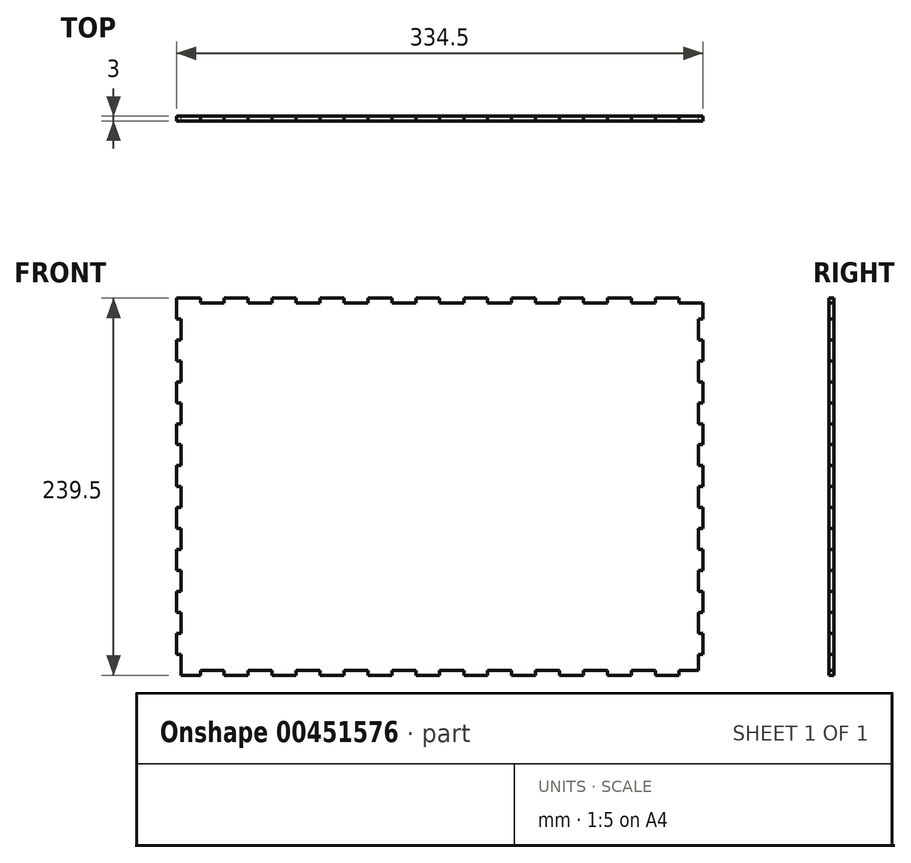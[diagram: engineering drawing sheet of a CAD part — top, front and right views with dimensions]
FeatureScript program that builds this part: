
annotation { "Feature Type Name" : "Feature", "Feature Type Description" : "" }
export const myFeature = defineFeature(function(context is Context, id is Id, definition is map)
    precondition{}
    {
        {
            var Q0;
            Q0=qCreatedBy(makeId("Front.planeOp"),FACE);
            var sketch = newSketch(context, id + "F0", { "sketchPlane" : qUnion([Q0])});
            skLineSegment(sketch, "E0.top", {"start": v(152.05, 119.75) * mm, "end": v(136.85, 119.75) * mm});
            skLineSegment(sketch, "E0.left", {"start": v(167.25, -117) * mm, "end": v(167.25, -116.75) * mm});
            skLineSegment(sketch, "E0.right", {"start": v(-167.25, -106.45) * mm, "end": v(-167.25, -93.15) * mm});
            skPoint(sketch, "E0.middle", {"position": v(0, 0) * mm});
            skLineSegment(sketch, "E1", {"start": v(-152.05, 116.75) * mm, "end": v(-136.85, 116.75) * mm});
            skLineSegment(sketch, "E2", {"start": v(-152.05, 119.75) * mm, "end": v(-152.05, 116.75) * mm});
            skLineSegment(sketch, "E3", {"start": v(-136.85, 119.75) * mm, "end": v(-136.85, 116.75) * mm});
            skLineSegment(sketch, "E4", {"start": v(-106.45, 119.75) * mm, "end": v(-106.45, 116.75) * mm});
            skLineSegment(sketch, "E5", {"start": v(-91.25, 119.75) * mm, "end": v(-91.25, 116.75) * mm});
            skLineSegment(sketch, "E6", {"start": v(-76.05, 119.75) * mm, "end": v(-76.05, 116.75) * mm});
            skLineSegment(sketch, "E7", {"start": v(-60.85, 119.75) * mm, "end": v(-60.85, 116.75) * mm});
            skLineSegment(sketch, "E8", {"start": v(-30.45, 119.75) * mm, "end": v(-30.45, 116.75) * mm});
            skLineSegment(sketch, "E9", {"start": v(-15.25, 119.75) * mm, "end": v(-15.25, 116.75) * mm});
            skLineSegment(sketch, "E10", {"start": v(-121.65, 119.75) * mm, "end": v(-121.65, 116.75) * mm});
            skLineSegment(sketch, "E11", {"start": v(-45.65, 119.75) * mm, "end": v(-45.65, 116.75) * mm});
            skLineSegment(sketch, "E12", {"start": v(-0.05, 119.75) * mm, "end": v(-0.05, 116.75) * mm});
            skLineSegment(sketch, "E13.MirrorCS", {"start": v(76.05, 119.75) * mm, "end": v(76.05, 116.75) * mm});
            skLineSegment(sketch, "E14.MirrorCS", {"start": v(60.85, 119.75) * mm, "end": v(60.85, 116.75) * mm});
            skLineSegment(sketch, "E15.MirrorCS", {"start": v(30.45, 119.75) * mm, "end": v(30.45, 116.75) * mm});
            skLineSegment(sketch, "E16.MirrorCS", {"start": v(121.65, 119.75) * mm, "end": v(121.65, 116.75) * mm});
            skLineSegment(sketch, "E17.MirrorCS", {"start": v(45.65, 119.75) * mm, "end": v(45.65, 116.75) * mm});
            skLineSegment(sketch, "E18.MirrorCS", {"start": v(0.05, 119.75) * mm, "end": v(0.05, 116.75) * mm});
            skLineSegment(sketch, "E19.MirrorCS", {"start": v(152.05, 119.75) * mm, "end": v(152.05, 116.75) * mm});
            skLineSegment(sketch, "E20.MirrorCS", {"start": v(15.25, 119.75) * mm, "end": v(15.25, 116.75) * mm});
            skLineSegment(sketch, "E21.MirrorCS", {"start": v(136.85, 119.75) * mm, "end": v(136.85, 116.75) * mm});
            skLineSegment(sketch, "E22.MirrorCS", {"start": v(106.45, 119.75) * mm, "end": v(106.45, 116.75) * mm});
            skLineSegment(sketch, "E23.MirrorCS", {"start": v(91.25, 119.75) * mm, "end": v(91.25, 116.75) * mm});
            skLineSegment(sketch, "E24.MirrorCS", {"start": v(-167.25, 119.75) * mm, "end": v(-152.05, 119.75) * mm});
            skLineSegment(sketch, "E25.trimOffspring", {"start": v(-0.05, 119.75) * mm, "end": v(0.05, 119.75) * mm});
            skLineSegment(sketch, "E26.trimOffspring", {"start": v(-121.65, 119.75) * mm, "end": v(-136.85, 119.75) * mm});
            skLineSegment(sketch, "E27.trimOffspring", {"start": v(-0.05, 116.75) * mm, "end": v(0.05, 116.75) * mm});
            skLineSegment(sketch, "E28.trimOffspring", {"start": v(-106.45, 116.75) * mm, "end": v(-121.65, 116.75) * mm});
            skLineSegment(sketch, "E29.trimOffspring", {"start": v(-91.25, 119.75) * mm, "end": v(-106.45, 119.75) * mm});
            skLineSegment(sketch, "E30.trimOffspring", {"start": v(-76.05, 116.75) * mm, "end": v(-91.25, 116.75) * mm});
            skLineSegment(sketch, "E31.trimOffspring", {"start": v(-60.85, 119.75) * mm, "end": v(-76.05, 119.75) * mm});
            skLineSegment(sketch, "E32.trimOffspring", {"start": v(-30.45, 119.75) * mm, "end": v(-45.65, 119.75) * mm});
            skLineSegment(sketch, "E33.trimOffspring", {"start": v(-15.25, 116.75) * mm, "end": v(-30.45, 116.75) * mm});
            skLineSegment(sketch, "E34.trimOffspring", {"start": v(30.45, 116.75) * mm, "end": v(45.65, 116.75) * mm});
            skLineSegment(sketch, "E35.trimOffspring", {"start": v(0.05, 119.75) * mm, "end": v(-15.25, 119.75) * mm});
            skLineSegment(sketch, "E36.trimOffspring", {"start": v(15.25, 116.75) * mm, "end": v(-0.05, 116.75) * mm});
            skLineSegment(sketch, "E37.trimOffspring", {"start": v(30.45, 119.75) * mm, "end": v(15.25, 119.75) * mm});
            skLineSegment(sketch, "E38.trimOffspring", {"start": v(152.05, 116.75) * mm, "end": v(167.25, 116.75) * mm});
            skLineSegment(sketch, "E39.trimOffspring", {"start": v(60.85, 119.75) * mm, "end": v(45.65, 119.75) * mm});
            skLineSegment(sketch, "E40.trimOffspring", {"start": v(76.05, 116.75) * mm, "end": v(60.85, 116.75) * mm});
            skLineSegment(sketch, "E41.trimOffspring", {"start": v(91.25, 119.75) * mm, "end": v(76.05, 119.75) * mm});
            skLineSegment(sketch, "E42.trimOffspring", {"start": v(106.45, 116.75) * mm, "end": v(91.25, 116.75) * mm});
            skLineSegment(sketch, "E43.trimOffspring", {"start": v(121.65, 119.75) * mm, "end": v(106.45, 119.75) * mm});
            skLineSegment(sketch, "E44.trimOffspring", {"start": v(136.85, 116.75) * mm, "end": v(121.65, 116.75) * mm});
            skPoint(sketch, "E45.MirrorCS.start.orphan", {"position": v(167.25, 117) * mm});
            skPoint(sketch, "E46.orphan", {"position": v(167.25, 120) * mm});
            skPoint(sketch, "E47.orphan", {"position": v(167.25, 119.75) * mm});
            skLineSegment(sketch, "E48.MirrorCS", {"start": v(-0.05, -119.75) * mm, "end": v(-0.05, -116.75) * mm});
            skLineSegment(sketch, "E49.MirrorCS", {"start": v(0.05, -119.75) * mm, "end": v(0.05, -116.75) * mm});
            skLineSegment(sketch, "E50.MirrorCS", {"start": v(-0.05, -119.75) * mm, "end": v(0.05, -119.75) * mm});
            skLineSegment(sketch, "E51.MirrorCS", {"start": v(-0.05, -116.75) * mm, "end": v(0.05, -116.75) * mm});
            skLineSegment(sketch, "E52.MirrorCS", {"start": v(-164.25, -119.75) * mm, "end": v(-152.05, -119.75) * mm});
            skLineSegment(sketch, "E53.MirrorCS", {"start": v(121.65, -119.75) * mm, "end": v(121.65, -116.75) * mm});
            skLineSegment(sketch, "E54.MirrorCS", {"start": v(15.25, -119.75) * mm, "end": v(15.25, -116.75) * mm});
            skLineSegment(sketch, "E55.MirrorCS", {"start": v(-45.65, -119.75) * mm, "end": v(-45.65, -116.75) * mm});
            skLineSegment(sketch, "E56.MirrorCS", {"start": v(30.45, -119.75) * mm, "end": v(30.45, -116.75) * mm});
            skLineSegment(sketch, "E57.MirrorCS", {"start": v(-152.05, -119.75) * mm, "end": v(-152.05, -116.75) * mm});
            skLineSegment(sketch, "E58.MirrorCS", {"start": v(-136.85, -119.75) * mm, "end": v(-136.85, -116.75) * mm});
            skLineSegment(sketch, "E59.MirrorCS", {"start": v(-106.45, -119.75) * mm, "end": v(-106.45, -116.75) * mm});
            skLineSegment(sketch, "E60.MirrorCS", {"start": v(-91.25, -119.75) * mm, "end": v(-91.25, -116.75) * mm});
            skLineSegment(sketch, "E61.MirrorCS", {"start": v(-76.05, -119.75) * mm, "end": v(-76.05, -116.75) * mm});
            skLineSegment(sketch, "E62.MirrorCS", {"start": v(-60.85, -119.75) * mm, "end": v(-60.85, -116.75) * mm});
            skLineSegment(sketch, "E63.MirrorCS", {"start": v(-30.45, -119.75) * mm, "end": v(-30.45, -116.75) * mm});
            skLineSegment(sketch, "E64.MirrorCS", {"start": v(-15.25, -119.75) * mm, "end": v(-15.25, -116.75) * mm});
            skLineSegment(sketch, "E65.MirrorCS", {"start": v(-121.65, -119.75) * mm, "end": v(-121.65, -116.75) * mm});
            skLineSegment(sketch, "E66.MirrorCS", {"start": v(136.85, -119.75) * mm, "end": v(136.85, -116.75) * mm});
            skLineSegment(sketch, "E67.MirrorCS", {"start": v(106.45, -119.75) * mm, "end": v(106.45, -116.75) * mm});
            skLineSegment(sketch, "E68.MirrorCS", {"start": v(152.05, -119.75) * mm, "end": v(152.05, -116.75) * mm});
            skLineSegment(sketch, "E69.MirrorCS", {"start": v(76.05, -119.75) * mm, "end": v(76.05, -116.75) * mm});
            skLineSegment(sketch, "E70.MirrorCS", {"start": v(152.05, -116.75) * mm, "end": v(164.25, -116.75) * mm});
            skLineSegment(sketch, "E71.MirrorCS", {"start": v(91.25, -119.75) * mm, "end": v(91.25, -116.75) * mm});
            skLineSegment(sketch, "E72.MirrorCS", {"start": v(60.85, -119.75) * mm, "end": v(60.85, -116.75) * mm});
            skLineSegment(sketch, "E73.MirrorCS", {"start": v(45.65, -119.75) * mm, "end": v(45.65, -116.75) * mm});
            skPoint(sketch, "E74.MirrorP", {"position": v(167.25, -120) * mm});
            skLineSegment(sketch, "E75.MirrorCS", {"start": v(60.85, -119.75) * mm, "end": v(45.65, -119.75) * mm});
            skLineSegment(sketch, "E76.MirrorCS", {"start": v(-106.45, -116.75) * mm, "end": v(-121.65, -116.75) * mm});
            skLineSegment(sketch, "E77.MirrorCS", {"start": v(0.05, -119.75) * mm, "end": v(-15.25, -119.75) * mm});
            skLineSegment(sketch, "E78.MirrorCS", {"start": v(136.85, -116.75) * mm, "end": v(121.65, -116.75) * mm});
            skLineSegment(sketch, "E79.MirrorCS", {"start": v(-30.45, -119.75) * mm, "end": v(-45.65, -119.75) * mm});
            skLineSegment(sketch, "E80.MirrorCS", {"start": v(152.05, -119.75) * mm, "end": v(136.85, -119.75) * mm});
            skLineSegment(sketch, "E81.MirrorCS", {"start": v(-152.05, -116.75) * mm, "end": v(-136.85, -116.75) * mm});
            skLineSegment(sketch, "E82.MirrorCS", {"start": v(76.05, -116.75) * mm, "end": v(60.85, -116.75) * mm});
            skLineSegment(sketch, "E83.MirrorCS", {"start": v(15.25, -116.75) * mm, "end": v(-0.05, -116.75) * mm});
            skLineSegment(sketch, "E84.MirrorCS", {"start": v(106.45, -116.75) * mm, "end": v(91.25, -116.75) * mm});
            skLineSegment(sketch, "E85.MirrorCS", {"start": v(30.45, -119.75) * mm, "end": v(15.25, -119.75) * mm});
            skLineSegment(sketch, "E86.MirrorCS", {"start": v(30.45, -116.75) * mm, "end": v(45.65, -116.75) * mm});
            skPoint(sketch, "E87.MirrorP", {"position": v(167.25, -117) * mm});
            skLineSegment(sketch, "E88.MirrorCS", {"start": v(91.25, -119.75) * mm, "end": v(76.05, -119.75) * mm});
            skLineSegment(sketch, "E89.MirrorCS", {"start": v(121.65, -119.75) * mm, "end": v(106.45, -119.75) * mm});
            skLineSegment(sketch, "E90.MirrorCS", {"start": v(-121.65, -119.75) * mm, "end": v(-136.85, -119.75) * mm});
            skLineSegment(sketch, "E91.MirrorCS", {"start": v(-15.25, -116.75) * mm, "end": v(-30.45, -116.75) * mm});
            skLineSegment(sketch, "E92.MirrorCS", {"start": v(-60.85, -119.75) * mm, "end": v(-76.05, -119.75) * mm});
            skLineSegment(sketch, "E93.MirrorCS", {"start": v(-76.05, -116.75) * mm, "end": v(-91.25, -116.75) * mm});
            skLineSegment(sketch, "E94.MirrorCS", {"start": v(-91.25, -119.75) * mm, "end": v(-106.45, -119.75) * mm});
            skPoint(sketch, "E95.MirrorP", {"position": v(167.25, -119.75) * mm});
            skLineSegment(sketch, "E96.trimOffspring", {"start": v(-45.65, 116.75) * mm, "end": v(-60.85, 116.75) * mm});
            skLineSegment(sketch, "E97.trimOffspring", {"start": v(-45.65, -116.75) * mm, "end": v(-60.85, -116.75) * mm});
            skLineSegment(sketch, "E98", {"start": v(-164.25, 26.65) * mm, "end": v(-164.25, 13.35) * mm});
            skLineSegment(sketch, "E99", {"start": v(-167.25, 106.45) * mm, "end": v(-164.25, 106.45) * mm});
            skLineSegment(sketch, "E100", {"start": v(-164.25, 93.15) * mm, "end": v(-167.25, 93.15) * mm});
            skLineSegment(sketch, "E101", {"start": v(-167.25, 79.85) * mm, "end": v(-164.25, 79.85) * mm});
            skLineSegment(sketch, "E102", {"start": v(-167.25, 66.55) * mm, "end": v(-164.25, 66.55) * mm});
            skLineSegment(sketch, "E103", {"start": v(-167.25, 53.25) * mm, "end": v(-164.25, 53.25) * mm});
            skLineSegment(sketch, "E104", {"start": v(-167.25, 39.95) * mm, "end": v(-164.25, 39.95) * mm});
            skLineSegment(sketch, "E105", {"start": v(-167.25, 26.65) * mm, "end": v(-164.25, 26.65) * mm});
            skLineSegment(sketch, "E106", {"start": v(-167.25, 13.35) * mm, "end": v(-164.25, 13.35) * mm});
            skLineSegment(sketch, "E107", {"start": v(-167.25, 0.05) * mm, "end": v(-164.25, 0.05) * mm});
            skLineSegment(sketch, "E108.MirrorCS", {"start": v(-167.25, -79.85) * mm, "end": v(-164.25, -79.85) * mm});
            skLineSegment(sketch, "E109.MirrorCS", {"start": v(-167.25, -0.05) * mm, "end": v(-164.25, -0.05) * mm});
            skLineSegment(sketch, "E110.MirrorCS", {"start": v(-167.25, -106.45) * mm, "end": v(-164.25, -106.45) * mm});
            skLineSegment(sketch, "E111.MirrorCS", {"start": v(-167.25, -13.35) * mm, "end": v(-164.25, -13.35) * mm});
            skLineSegment(sketch, "E112.MirrorCS", {"start": v(-167.25, -26.65) * mm, "end": v(-164.25, -26.65) * mm});
            skLineSegment(sketch, "E113.MirrorCS", {"start": v(-167.25, -53.25) * mm, "end": v(-164.25, -53.25) * mm});
            skLineSegment(sketch, "E114.MirrorCS", {"start": v(-167.25, -66.55) * mm, "end": v(-164.25, -66.55) * mm});
            skLineSegment(sketch, "E115.MirrorCS", {"start": v(-167.25, -39.95) * mm, "end": v(-164.25, -39.95) * mm});
            skLineSegment(sketch, "E116.MirrorCS", {"start": v(-164.25, -93.15) * mm, "end": v(-167.25, -93.15) * mm});
            skLineSegment(sketch, "E117.MirrorCS", {"start": v(-167.25, 119.75) * mm, "end": v(-167.25, 106.45) * mm});
            skLineSegment(sketch, "E118.MirrorCS", {"start": v(-164.25, -119.75) * mm, "end": v(-164.25, -106.45) * mm});
            skPoint(sketch, "E119.orphan", {"position": v(-164.25, 119.75) * mm});
            skLineSegment(sketch, "E120.trimOffspring", {"start": v(-167.25, 119.75) * mm, "end": v(-167.25, 120) * mm});
            skLineSegment(sketch, "E121.trimOffspring", {"start": v(-167.25, 93.15) * mm, "end": v(-167.25, 79.85) * mm});
            skLineSegment(sketch, "E122.trimOffspring", {"start": v(-164.25, 93.15) * mm, "end": v(-164.25, 106.45) * mm});
            skLineSegment(sketch, "E123.trimOffspring", {"start": v(-167.25, 66.55) * mm, "end": v(-167.25, 53.25) * mm});
            skLineSegment(sketch, "E124.trimOffspring", {"start": v(-164.25, 66.55) * mm, "end": v(-164.25, 79.85) * mm});
            skLineSegment(sketch, "E125.trimOffspring", {"start": v(-167.25, 39.95) * mm, "end": v(-167.25, 26.65) * mm});
            skLineSegment(sketch, "E126.trimOffspring", {"start": v(-164.25, 39.95) * mm, "end": v(-164.25, 53.25) * mm});
            skLineSegment(sketch, "E127.trimOffspring", {"start": v(-167.25, 13.35) * mm, "end": v(-167.25, -0.05) * mm});
            skLineSegment(sketch, "E128.trimOffspring", {"start": v(-164.25, 0.05) * mm, "end": v(-164.25, -0.05) * mm});
            skLineSegment(sketch, "E129.trimOffspring", {"start": v(-164.25, 13.35) * mm, "end": v(-164.25, 26.65) * mm});
            skLineSegment(sketch, "E130.trimOffspring", {"start": v(-167.25, -0.05) * mm, "end": v(-167.25, 0.05) * mm});
            skLineSegment(sketch, "E131.trimOffspring", {"start": v(-167.25, -119.75) * mm, "end": v(-167.25, -120) * mm});
            skLineSegment(sketch, "E132.trimOffspring", {"start": v(-164.25, -13.35) * mm, "end": v(-164.25, 0.05) * mm});
            skLineSegment(sketch, "E133.trimOffspring", {"start": v(-167.25, -26.65) * mm, "end": v(-167.25, -13.35) * mm});
            skLineSegment(sketch, "E134.trimOffspring", {"start": v(-164.25, -39.95) * mm, "end": v(-164.25, -26.65) * mm});
            skLineSegment(sketch, "E135.trimOffspring", {"start": v(-167.25, -53.25) * mm, "end": v(-167.25, -39.95) * mm});
            skLineSegment(sketch, "E136.trimOffspring", {"start": v(-164.25, -66.55) * mm, "end": v(-164.25, -53.25) * mm});
            skLineSegment(sketch, "E137.trimOffspring", {"start": v(-167.25, -79.85) * mm, "end": v(-167.25, -66.55) * mm});
            skLineSegment(sketch, "E138.trimOffspring", {"start": v(-164.25, -93.15) * mm, "end": v(-164.25, -79.85) * mm});
            skPoint(sketch, "E139.orphan", {"position": v(-167.25, -119.75) * mm});
            skLineSegment(sketch, "E140.MirrorCS", {"start": v(167.25, 0.05) * mm, "end": v(164.25, 0.05) * mm});
            skLineSegment(sketch, "E141.MirrorCS", {"start": v(167.25, -0.05) * mm, "end": v(167.25, 0.05) * mm});
            skLineSegment(sketch, "E142.MirrorCS", {"start": v(167.25, -0.05) * mm, "end": v(164.25, -0.05) * mm});
            skLineSegment(sketch, "E143.MirrorCS", {"start": v(164.25, 0.05) * mm, "end": v(164.25, -0.05) * mm});
            skLineSegment(sketch, "E144.MirrorCS", {"start": v(164.25, 13.35) * mm, "end": v(164.25, 26.65) * mm});
            skLineSegment(sketch, "E145.MirrorCS", {"start": v(167.25, 119.75) * mm, "end": v(167.25, 120) * mm});
            skLineSegment(sketch, "E146.MirrorCS", {"start": v(164.25, 26.65) * mm, "end": v(164.25, 13.35) * mm});
            skLineSegment(sketch, "E147.MirrorCS", {"start": v(167.25, 26.65) * mm, "end": v(164.25, 26.65) * mm});
            skLineSegment(sketch, "E148.MirrorCS", {"start": v(167.25, 13.35) * mm, "end": v(164.25, 13.35) * mm});
            skLineSegment(sketch, "E149.MirrorCS", {"start": v(167.25, -119.75) * mm, "end": v(167.25, -120) * mm});
            skLineSegment(sketch, "E150.MirrorCS", {"start": v(167.25, 79.85) * mm, "end": v(164.25, 79.85) * mm});
            skLineSegment(sketch, "E151.MirrorCS", {"start": v(164.25, -93.15) * mm, "end": v(167.25, -93.15) * mm});
            skLineSegment(sketch, "E152.MirrorCS", {"start": v(164.25, -39.95) * mm, "end": v(164.25, -26.65) * mm});
            skLineSegment(sketch, "E153.MirrorCS", {"start": v(167.25, 117) * mm, "end": v(167.25, 106.45) * mm});
            skLineSegment(sketch, "E154.MirrorCS", {"start": v(167.25, 66.55) * mm, "end": v(164.25, 66.55) * mm});
            skLineSegment(sketch, "E155.MirrorCS", {"start": v(167.25, 53.25) * mm, "end": v(164.25, 53.25) * mm});
            skLineSegment(sketch, "E156.MirrorCS", {"start": v(167.25, -26.65) * mm, "end": v(164.25, -26.65) * mm});
            skLineSegment(sketch, "E157.MirrorCS", {"start": v(164.25, -66.55) * mm, "end": v(164.25, -53.25) * mm});
            skLineSegment(sketch, "E158.MirrorCS", {"start": v(167.25, 39.95) * mm, "end": v(164.25, 39.95) * mm});
            skLineSegment(sketch, "E159.MirrorCS", {"start": v(167.25, -53.25) * mm, "end": v(164.25, -53.25) * mm});
            skLineSegment(sketch, "E160.MirrorCS", {"start": v(164.25, 93.15) * mm, "end": v(164.25, 106.45) * mm});
            skLineSegment(sketch, "E161.MirrorCS", {"start": v(164.25, -93.15) * mm, "end": v(164.25, -79.85) * mm});
            skLineSegment(sketch, "E162.MirrorCS", {"start": v(167.25, -79.85) * mm, "end": v(164.25, -79.85) * mm});
            skLineSegment(sketch, "E163.MirrorCS", {"start": v(164.25, 66.55) * mm, "end": v(164.25, 79.85) * mm});
            skLineSegment(sketch, "E164.MirrorCS", {"start": v(167.25, -66.55) * mm, "end": v(164.25, -66.55) * mm});
            skLineSegment(sketch, "E165.MirrorCS", {"start": v(167.25, 106.45) * mm, "end": v(164.25, 106.45) * mm});
            skLineSegment(sketch, "E166.MirrorCS", {"start": v(164.25, 39.95) * mm, "end": v(164.25, 53.25) * mm});
            skLineSegment(sketch, "E167.MirrorCS", {"start": v(167.25, -106.45) * mm, "end": v(164.25, -106.45) * mm});
            skLineSegment(sketch, "E168.MirrorCS", {"start": v(167.25, -13.35) * mm, "end": v(164.25, -13.35) * mm});
            skLineSegment(sketch, "E169.MirrorCS", {"start": v(164.25, -13.35) * mm, "end": v(164.25, 0.05) * mm});
            skLineSegment(sketch, "E170.MirrorCS", {"start": v(167.25, -39.95) * mm, "end": v(164.25, -39.95) * mm});
            skLineSegment(sketch, "E171.MirrorCS", {"start": v(164.25, 93.15) * mm, "end": v(167.25, 93.15) * mm});
            skLineSegment(sketch, "E172.MirrorCS", {"start": v(164.25, -116.75) * mm, "end": v(164.25, -106.45) * mm});
            skPoint(sketch, "E173.MirrorP", {"position": v(164.25, 119.75) * mm});
            skLineSegment(sketch, "E174.MirrorCS", {"start": v(167.25, 13.35) * mm, "end": v(167.25, -0.05) * mm});
            skLineSegment(sketch, "E175.MirrorCS", {"start": v(167.25, -53.25) * mm, "end": v(167.25, -39.95) * mm});
            skLineSegment(sketch, "E176.MirrorCS", {"start": v(167.25, -79.85) * mm, "end": v(167.25, -66.55) * mm});
            skLineSegment(sketch, "E177.MirrorCS", {"start": v(167.25, 66.55) * mm, "end": v(167.25, 53.25) * mm});
            skLineSegment(sketch, "E178.MirrorCS", {"start": v(167.25, -106.45) * mm, "end": v(167.25, -93.15) * mm});
            skLineSegment(sketch, "E179.MirrorCS", {"start": v(167.25, 39.95) * mm, "end": v(167.25, 26.65) * mm});
            skLineSegment(sketch, "E180.MirrorCS", {"start": v(167.25, -26.65) * mm, "end": v(167.25, -13.35) * mm});
            skLineSegment(sketch, "E181.trimOffspring", {"start": v(167.25, 106.45) * mm, "end": v(167.25, 117) * mm});
            skLineSegment(sketch, "E182.trimOffspring", {"start": v(167.25, 79.85) * mm, "end": v(167.25, 93.15) * mm});
            skLineSegment(sketch, "E183.trimOffspring", {"start": v(167.25, 53.25) * mm, "end": v(167.25, 66.55) * mm});
            skLineSegment(sketch, "E184.trimOffspring", {"start": v(167.25, 26.65) * mm, "end": v(167.25, 39.95) * mm});
            skLineSegment(sketch, "E185.trimOffspring", {"start": v(167.25, -0.05) * mm, "end": v(167.25, 13.35) * mm});
            skPoint(sketch, "E186.orphan", {"position": v(164.25, -119.75) * mm});
            skSolve(sketch);
        }
        {
            var Q0;
            Q0=makeQuery(id+"F0.imprint","IMPRINT",FACE,{"disambiguationData":[TD([[makeQuery(id+"F0.imprint","IMPRINT",EDGE,{"derivedFrom":sQuery(id+"F0.wireOp",EDGE,"E0.top")}),1.0]])]});
            extrude(context, id + "F1", {"entities" : qUnion([Q0]), "depth" : 3 * mm, "offsetDistance" : 25 * mm});
        }
    });
